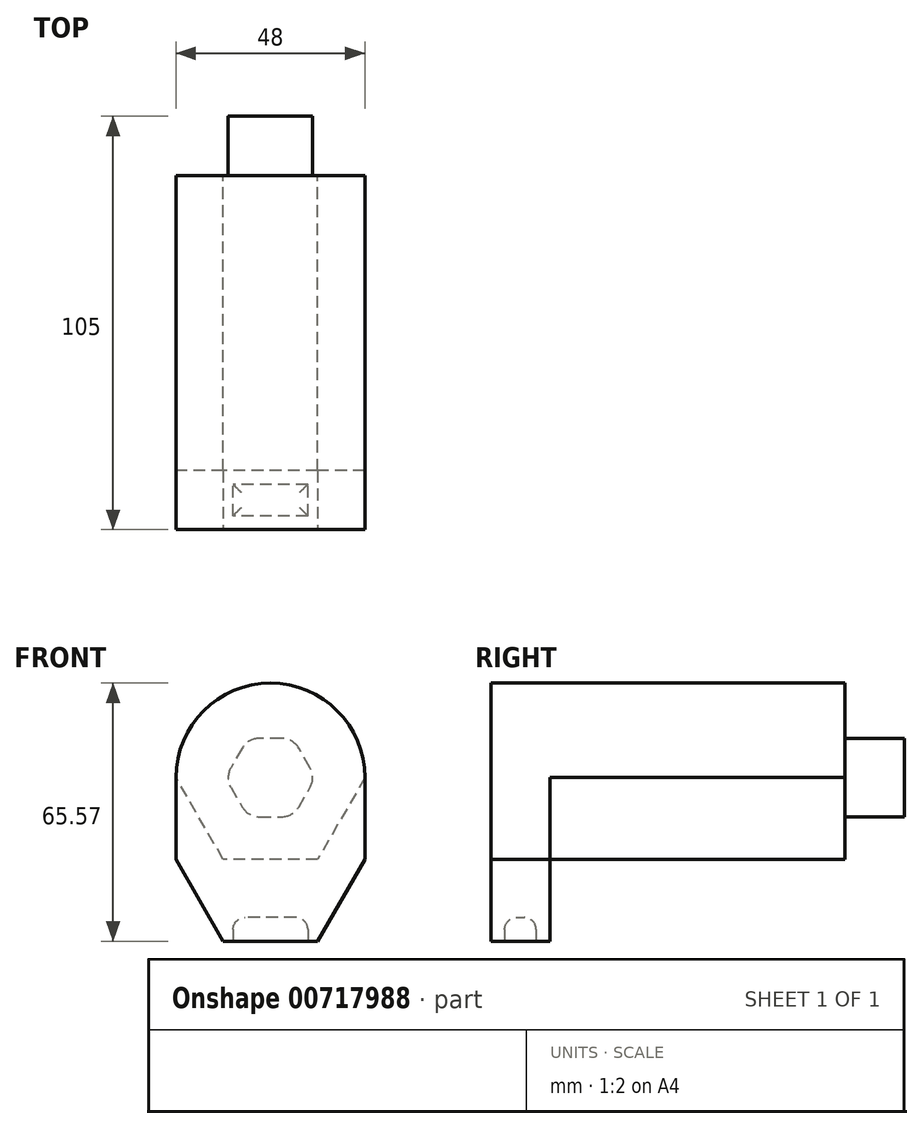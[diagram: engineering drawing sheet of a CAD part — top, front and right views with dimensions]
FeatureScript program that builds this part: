
annotation { "Feature Type Name" : "Feature", "Feature Type Description" : "" }
export const myFeature = defineFeature(function(context is Context, id is Id, definition is map)
    precondition{}
    {
        {
            var Q0;
            Q0=qCreatedBy(makeId("Front.planeOp"),FACE);
            var sketch = newSketch(context, id + "F0", { "sketchPlane" : qUnion([Q0])});
            skCircle(sketch, "E0.cCircle", {"center": v(0, 0) * mm, "radius": 24 * mm, "construction": true});
            skLineSegment(sketch, "E0.0", {"start": v(24, 0) * mm, "end": v(12, -20.78) * mm});
            skLineSegment(sketch, "E0.1", {"start": v(12, -20.78) * mm, "end": v(-12, -20.78) * mm});
            skLineSegment(sketch, "E0.2", {"start": v(-12, -20.78) * mm, "end": v(-24, 0) * mm});
            skLineSegment(sketch, "E0.3", {"start": v(-24, 0) * mm, "end": v(-12, 20.78) * mm});
            skLineSegment(sketch, "E0.4", {"start": v(-12, 20.78) * mm, "end": v(12, 20.78) * mm});
            skLineSegment(sketch, "E0.5", {"start": v(12, 20.78) * mm, "end": v(24, 0) * mm});
            skArc(sketch, "E1", {"start": v(24, 0) * mm, "mid": v(0, 24) * mm, "end": v(-24, 0) * mm});
            skSolve(sketch);
        }
        {
            var Q0;
            Q0 = qSketchRegion(id + "F0", true);
            extrude(context, id + "F1", {"entities" : qUnion([Q0]), "endBound" : BoundingType.SYMMETRIC, "depth" : 90 * mm, "offsetDistance" : 25 * mm});
        }
        {
            var Q0;
            Q0=makeQuery(id+"F1.opExtrude","CAP_FACE",FACE,{"disambiguationData":[OSD([sQuery(id+"F0.wireOp",EDGE,"E0.0"),sQuery(id+"F0.wireOp",EDGE,"E0.1"),sQuery(id+"F0.wireOp",EDGE,"E0.2"),sQuery(id+"F0.wireOp",EDGE,"E1")])],"isStart":false});
            var sketch = newSketch(context, id + "F2", { "sketchPlane" : qUnion([Q0])});
            skCircle(sketch, "E2.cCircle", {"center": v(0, -20.78) * mm, "radius": 24 * mm, "construction": true});
            skLineSegment(sketch, "E2.0", {"start": v(12, -41.57) * mm, "end": v(-12, -41.57) * mm});
            skLineSegment(sketch, "E2.1", {"start": v(-12, -41.57) * mm, "end": v(-24, -20.78) * mm});
            skLineSegment(sketch, "E2.2", {"start": v(-24, -20.78) * mm, "end": v(-12, 0) * mm});
            skLineSegment(sketch, "E2.3", {"start": v(-12, 0) * mm, "end": v(12, 0) * mm});
            skLineSegment(sketch, "E2.4", {"start": v(12, 0) * mm, "end": v(24, -20.78) * mm});
            skLineSegment(sketch, "E2.5", {"start": v(24, -20.78) * mm, "end": v(12, -41.57) * mm});
            skLineSegment(sketch, "E3", {"start": v(-24, 0) * mm, "end": v(-24, -20.78) * mm});
            skLineSegment(sketch, "E4", {"start": v(24, -20.78) * mm, "end": v(24, 0) * mm});
            skSolve(sketch);
        }
        {
            var Q0;
            Q0 = qSketchRegion(id + "F2", true);
            var Q1;
            {var subQ0=sQuery(id+"F2.wireOp",EDGE,"E3");Q1=makeQuery(id+"F2.imprint","IMPRINT",FACE,{"disambiguationData":[TD([[makeQuery(id+"F2.imprint","IMPRINT",EDGE,{"derivedFrom":subQ0}),1.0]])]});}
            var Q2;
            {var subQ0=sQuery(id+"F2.wireOp",EDGE,"E4");Q2=makeQuery(id+"F2.imprint","IMPRINT",FACE,{"disambiguationData":[TD([[makeQuery(id+"F2.imprint","IMPRINT",EDGE,{"derivedFrom":subQ0}),1.0]])]});}
            extrude(context, id + "F3", {"entities" : qUnion([Q0, Q1, Q2]), "operationType" : NewBodyOperationType.ADD, "oppositeDirection" : true, "depth" : 15 * mm, "offsetDistance" : 25 * mm});
        }
        {
            var Q0;
            Q0=makeQuery(id+"F3.opExtrude","SWEPT_FACE",FACE,{"disambiguationData":[OSD([sQuery(id+"F2.wireOp",EDGE,"E2.0")])]});
            var sketch = newSketch(context, id + "F4", { "sketchPlane" : qUnion([Q0])});
            skLineSegment(sketch, "E5.bottom", {"start": v(9.5, 41.5) * mm, "end": v(-9.5, 41.5) * mm});
            skLineSegment(sketch, "E5.top", {"start": v(9.5, 33.5) * mm, "end": v(-9.5, 33.5) * mm});
            skLineSegment(sketch, "E5.left", {"start": v(9.5, 41.5) * mm, "end": v(9.5, 33.5) * mm});
            skLineSegment(sketch, "E5.right", {"start": v(-9.5, 41.5) * mm, "end": v(-9.5, 33.5) * mm});
            skPoint(sketch, "E5.middle", {"position": v(0, 37.5) * mm});
            skPoint(sketch, "E5.middle.positionSnap0", {"position": v(-12, 37.5) * mm});
            skPoint(sketch, "E5.centerSnap0", {"position": v(-12, 37.5) * mm});
            skSolve(sketch);
        }
        {
            var Q0;
            Q0 = qSketchRegion(id + "F4", true);
            extrude(context, id + "F5", {"entities" : qUnion([Q0]), "operationType" : NewBodyOperationType.REMOVE, "oppositeDirection" : true, "depth" : 6 * mm, "offsetDistance" : 25 * mm});
        }
        {
            var Q0;
            Q0=makeQuery(id+"F1.opExtrude","CAP_FACE",FACE,{"disambiguationData":[OSD([sQuery(id+"F0.wireOp",EDGE,"E0.0"),sQuery(id+"F0.wireOp",EDGE,"E0.1"),sQuery(id+"F0.wireOp",EDGE,"E0.2"),sQuery(id+"F0.wireOp",EDGE,"E1")])],"isStart":true});
            var sketch = newSketch(context, id + "F6", { "sketchPlane" : qUnion([Q0])});
            skCircle(sketch, "E6.cCircle", {"center": v(0, 0) * mm, "radius": 11.5 * mm, "construction": true});
            skLineSegment(sketch, "E6.0", {"start": v(11.5, 0) * mm, "end": v(5.75, -9.96) * mm});
            skLineSegment(sketch, "E6.1", {"start": v(5.75, -9.96) * mm, "end": v(-5.75, -9.96) * mm});
            skLineSegment(sketch, "E6.2", {"start": v(-5.75, -9.96) * mm, "end": v(-11.5, 0) * mm});
            skLineSegment(sketch, "E6.3", {"start": v(-11.5, 0) * mm, "end": v(-5.75, 9.96) * mm});
            skLineSegment(sketch, "E6.4", {"start": v(-5.75, 9.96) * mm, "end": v(5.75, 9.96) * mm});
            skLineSegment(sketch, "E6.5", {"start": v(5.75, 9.96) * mm, "end": v(11.5, 0) * mm});
            skSolve(sketch);
        }
        {
            var Q0;
            Q0 = qSketchRegion(id + "F6", true);
            extrude(context, id + "F7", {"entities" : qUnion([Q0]), "operationType" : NewBodyOperationType.ADD, "depth" : 15 * mm, "offsetDistance" : 25 * mm});
        }
        {
            var Q0;
            Q0=makeQuery(id+"F5.boolean.opBoolean","COPY",FACE,{"derivedFrom":makeQuery(id+"F5.opExtrude","CAP_FACE",FACE,{"disambiguationData":[OSD([sQuery(id+"F4.wireOp",EDGE,"E5.bottom"),sQuery(id+"F4.wireOp",EDGE,"E5.top"),sQuery(id+"F4.wireOp",EDGE,"E5.left"),sQuery(id+"F4.wireOp",EDGE,"E5.right")])],"isStart":false})});
            fillet(context, id + "F8", {"entities" : qUnion([Q0]), "radius" : 3 * mm, "tangentPropagation" : true, "allowEdgeOverflow" : false});
        }
        {
            var Q0;
            Q0=makeQuery(id+"F7.opExtrude","SWEPT_EDGE",EDGE,{"disambiguationData":[OSD([sQuery(id+"F6.wireOp",EDGE,"E6.2"),sQuery(id+"F6.wireOp",EDGE,"E6.3")])]});
            var Q1;
            Q1=makeQuery(id+"F7.opExtrude","SWEPT_EDGE",EDGE,{"disambiguationData":[OSD([sQuery(id+"F6.wireOp",EDGE,"E6.3"),sQuery(id+"F6.wireOp",EDGE,"E6.4")])]});
            var Q2;
            Q2=makeQuery(id+"F7.opExtrude","SWEPT_EDGE",EDGE,{"disambiguationData":[OSD([sQuery(id+"F6.wireOp",EDGE,"E6.4"),sQuery(id+"F6.wireOp",EDGE,"E6.5")])]});
            var Q3;
            Q3=makeQuery(id+"F7.opExtrude","SWEPT_EDGE",EDGE,{"disambiguationData":[OSD([sQuery(id+"F6.wireOp",EDGE,"E6.0"),sQuery(id+"F6.wireOp",EDGE,"E6.5")])]});
            var Q4;
            Q4=makeQuery(id+"F7.opExtrude","SWEPT_EDGE",EDGE,{"disambiguationData":[OSD([sQuery(id+"F6.wireOp",EDGE,"E6.0"),sQuery(id+"F6.wireOp",EDGE,"E6.1")])]});
            var Q5;
            Q5=makeQuery(id+"F7.opExtrude","SWEPT_EDGE",EDGE,{"disambiguationData":[OSD([sQuery(id+"F6.wireOp",EDGE,"E6.1"),sQuery(id+"F6.wireOp",EDGE,"E6.2")])]});
            fillet(context, id + "F9", {"entities" : qUnion([Q0, Q1, Q2, Q3, Q4, Q5]), "radius" : 5 * mm, "tangentPropagation" : true, "allowEdgeOverflow" : false});
        }
    });
